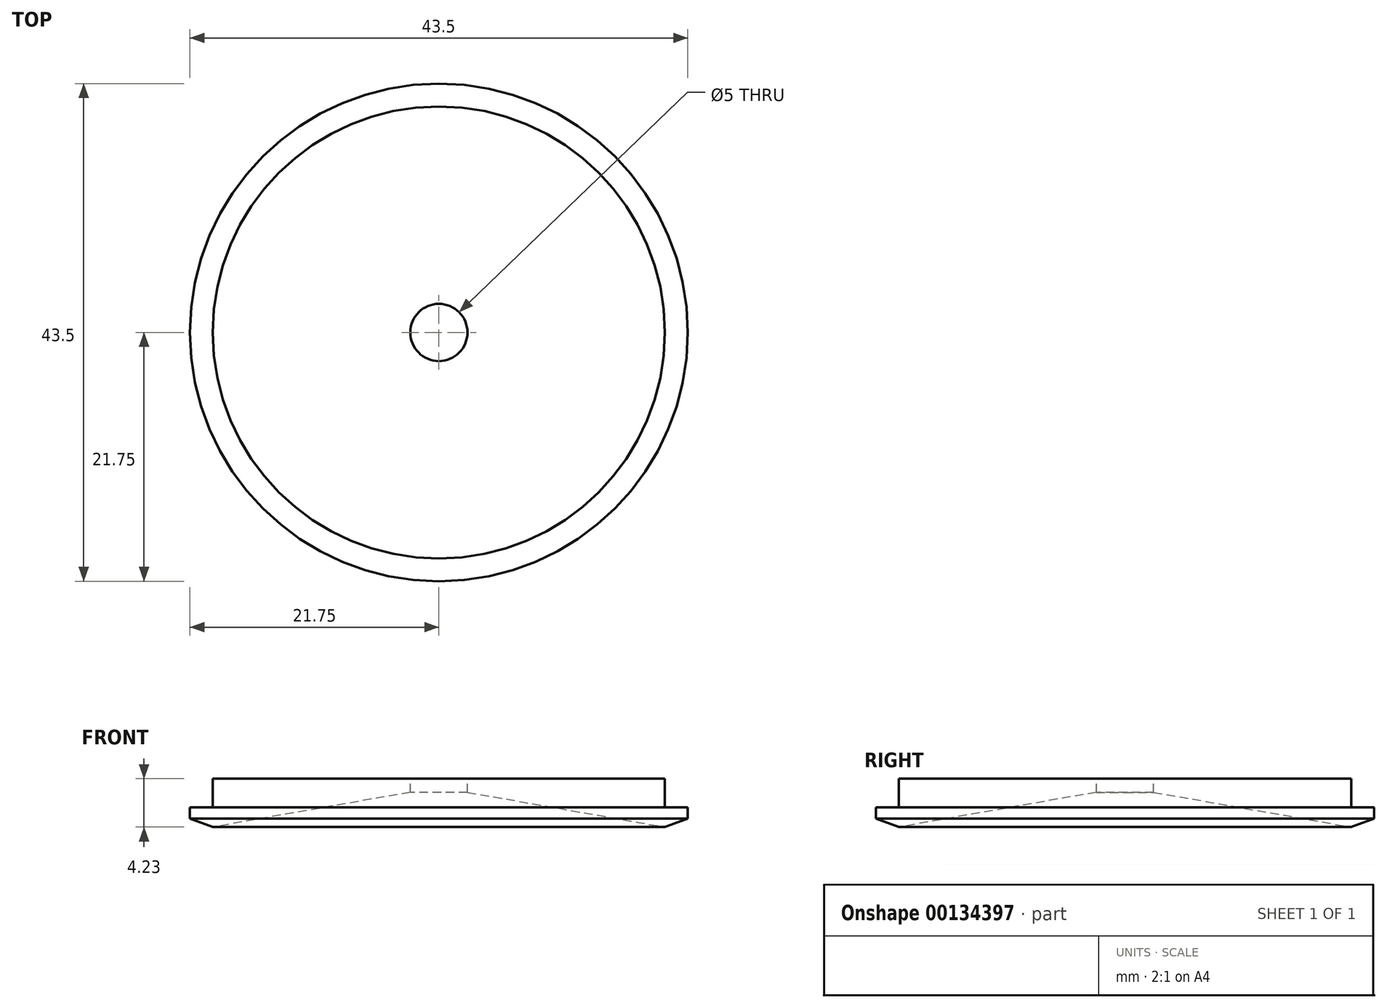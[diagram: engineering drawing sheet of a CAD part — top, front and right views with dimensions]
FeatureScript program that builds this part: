
annotation { "Feature Type Name" : "Feature", "Feature Type Description" : "" }
export const myFeature = defineFeature(function(context is Context, id is Id, definition is map)
    precondition{}
    {
        {
            var Q0;
            Q0=qCreatedBy(makeId("Front.planeOp"),FACE);
            var sketch = newSketch(context, id + "F0", { "sketchPlane" : qUnion([Q0])});
            skLineSegment(sketch, "E0", {"start": v(0, 0) * mm, "end": v(-21.75, 0) * mm, "construction": true});
            skLineSegment(sketch, "E1", {"start": v(-21.75, 0) * mm, "end": v(-21.75, 1) * mm, "construction": true});
            skLineSegment(sketch, "E2", {"start": v(-21.75, 1) * mm, "end": v(-19.75, 1) * mm, "construction": true});
            skLineSegment(sketch, "E3", {"start": v(-19.75, 1) * mm, "end": v(-19.75, 3.5) * mm, "construction": true});
            skLineSegment(sketch, "E4", {"start": v(-19.75, 1) * mm, "end": v(-19.75, 0) * mm, "construction": true});
            skLineSegment(sketch, "E5", {"start": v(-2.5, 2.31) * mm, "end": v(0, 2.31) * mm, "construction": true});
            skLineSegment(sketch, "E6", {"start": v(0, 2.31) * mm, "end": v(0, 0) * mm, "construction": true});
            skLineSegment(sketch, "E7", {"start": v(-21.75, 0) * mm, "end": v(-19.75, -0.73) * mm, "construction": true});
            skLineSegment(sketch, "E8", {"start": v(-19.75, -0.73) * mm, "end": v(-19.75, 0) * mm, "construction": true});
            skLineSegment(sketch, "E9", {"start": v(-19.75, -0.73) * mm, "end": v(-2.5, 2.31) * mm, "construction": true});
            skLineSegment(sketch, "E10", {"start": v(-2.5, 2.31) * mm, "end": v(-2.5, 3.5) * mm, "construction": true});
            skLineSegment(sketch, "E11", {"start": v(-2.5, 3.5) * mm, "end": v(-19.75, 3.5) * mm, "construction": true});
            skLineSegment(sketch, "E12", {"start": v(-2.5, 2.31) * mm, "end": v(-19.75, -0.73) * mm});
            skLineSegment(sketch, "E13", {"start": v(-19.75, -0.73) * mm, "end": v(-21.75, 0) * mm});
            skLineSegment(sketch, "E14", {"start": v(-21.75, 0) * mm, "end": v(-21.75, 1) * mm});
            skLineSegment(sketch, "E15", {"start": v(-21.75, 1) * mm, "end": v(-19.75, 1) * mm});
            skLineSegment(sketch, "E16", {"start": v(-19.75, 1) * mm, "end": v(-19.75, 3.5) * mm});
            skLineSegment(sketch, "E17", {"start": v(-19.75, 3.5) * mm, "end": v(-2.5, 3.5) * mm});
            skLineSegment(sketch, "E18", {"start": v(-2.5, 3.5) * mm, "end": v(-2.5, 2.31) * mm});
            skSolve(sketch);
        }
        {
            var Q0;
            Q0=makeQuery(id+"F0.imprint","IMPRINT",FACE,{"disambiguationData":[TD([[makeQuery(id+"F0.imprint","IMPRINT",EDGE,{"derivedFrom":sQuery(id+"F0.wireOp",EDGE,"E12")}),-1.0]])]});
            var Q1;
            Q1=sQuery(id+"F0.wireOp",EDGE,"E6");
            revolve(context, id + "F1", {"entities" : qUnion([Q0]), "axis" : qUnion([Q1]), "revolveType" : RevolveType.FULL});
        }
    });
